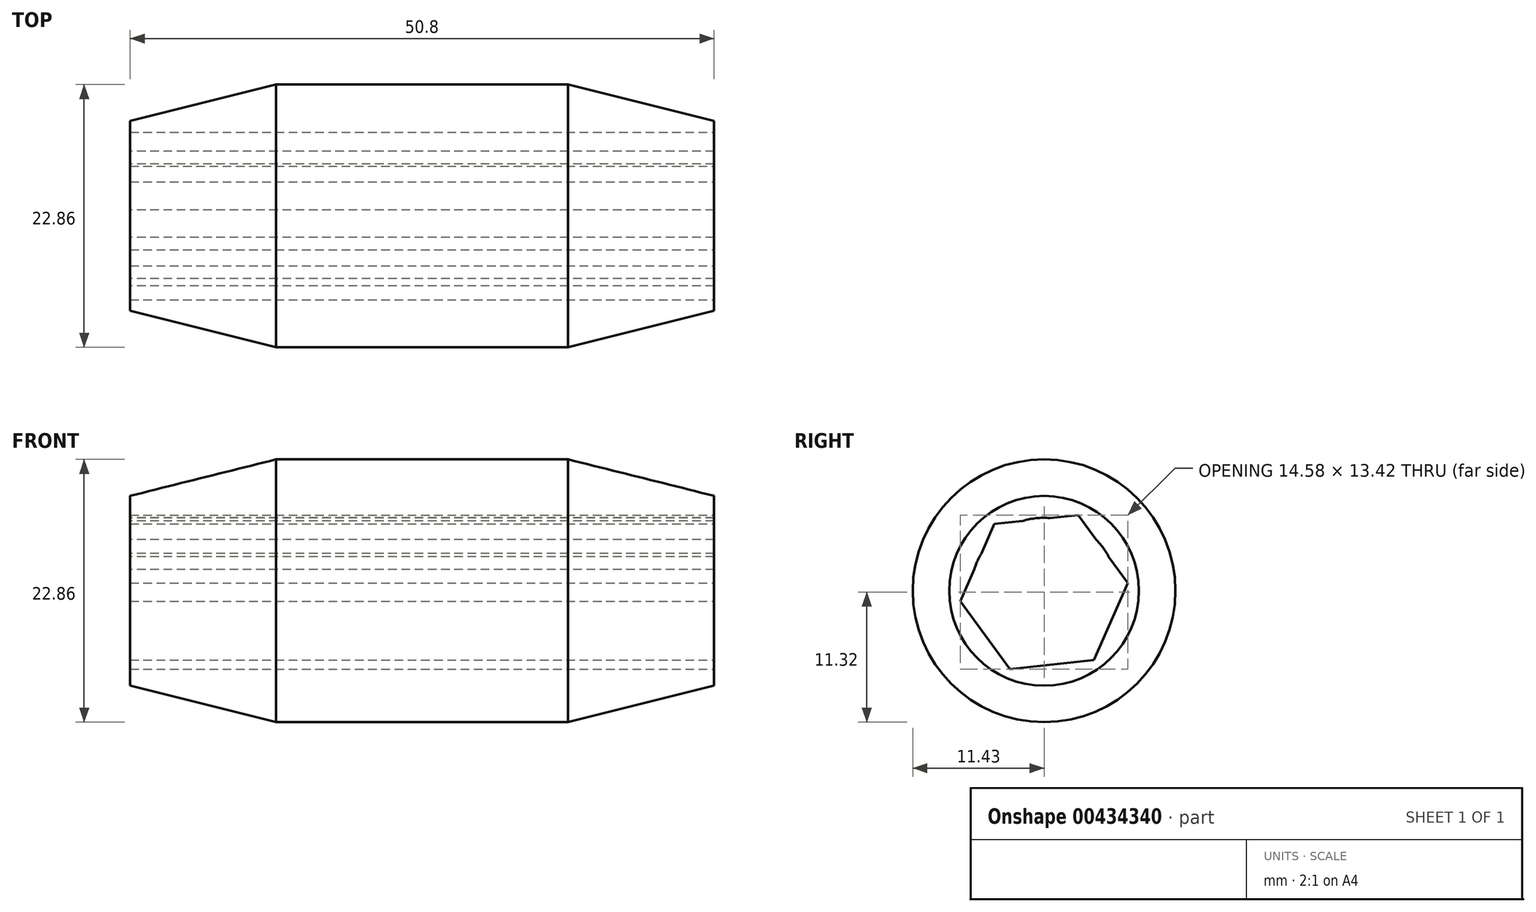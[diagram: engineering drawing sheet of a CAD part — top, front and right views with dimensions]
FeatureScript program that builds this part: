
annotation { "Feature Type Name" : "Feature", "Feature Type Description" : "" }
export const myFeature = defineFeature(function(context is Context, id is Id, definition is map)
    precondition{}
    {
        {
            var Q0;
            Q0=qCreatedBy(makeId("Right.planeOp"),FACE);
            var sketch = newSketch(context, id + "F0", { "sketchPlane" : qUnion([Q0])});
            skCircle(sketch, "E0.cCircle", {"center": v(0, 0) * mm, "radius": 6.35 * mm, "construction": true});
            skLineSegment(sketch, "E0.0", {"start": v(2.96, 6.7) * mm, "end": v(7.29, 0.8) * mm});
            skLineSegment(sketch, "E0.1", {"start": v(7.29, 0.8) * mm, "end": v(4.33, -5.92) * mm});
            skLineSegment(sketch, "E0.2", {"start": v(4.33, -5.92) * mm, "end": v(-2.96, -6.7) * mm});
            skLineSegment(sketch, "E0.3", {"start": v(-2.96, -6.7) * mm, "end": v(-7.29, -0.8) * mm});
            skLineSegment(sketch, "E0.4", {"start": v(-7.29, -0.8) * mm, "end": v(-4.33, 5.92) * mm});
            skLineSegment(sketch, "E0.5", {"start": v(-4.33, 5.92) * mm, "end": v(2.96, 6.7) * mm});
            skPoint(sketch, "E0.0.midPoint", {"position": v(5.12, 3.75) * mm});
            skSolve(sketch);
        }
        {
            var Q0;
            Q0=qCreatedBy(makeId("Front.planeOp"),FACE);
            var sketch = newSketch(context, id + "F1", { "sketchPlane" : qUnion([Q0])});
            skLineSegment(sketch, "E1", {"start": v(-42.82, 0.11) * mm, "end": v(41.93, 0.11) * mm, "construction": true});
            skLineSegment(sketch, "E2", {"start": v(-25.43, 6.46) * mm, "end": v(25.37, 6.46) * mm});
            skLineSegment(sketch, "E3", {"start": v(-12.73, 11.54) * mm, "end": v(12.67, 11.54) * mm});
            skLineSegment(sketch, "E4", {"start": v(-12.73, 11.54) * mm, "end": v(-25.43, 8.37) * mm});
            skLineSegment(sketch, "E5", {"start": v(12.67, 11.54) * mm, "end": v(25.37, 8.37) * mm});
            skLineSegment(sketch, "E6", {"start": v(25.37, 8.37) * mm, "end": v(25.37, 6.46) * mm});
            skLineSegment(sketch, "E7", {"start": v(-25.43, 8.37) * mm, "end": v(-25.43, 6.46) * mm});
            skSolve(sketch);
        }
        {
            var Q0;
            Q0 = qSketchRegion(id + "F1", true);
            var Q1;
            Q1=sQuery(id+"F1.wireOp",EDGE,"E1");
            revolve(context, id + "F2", {"entities" : qUnion([Q0]), "axis" : qUnion([Q1]), "revolveType" : RevolveType.FULL});
        }
        {
            var Q0;
            Q0 = qSketchRegion(id + "F0", true);
            extrude(context, id + "F3", {"entities" : qUnion([Q0]), "operationType" : NewBodyOperationType.REMOVE, "oppositeDirection" : true, "depth" : 38.1 * mm, "hasSecondDirection" : true, "secondDirectionOppositeDirection" : false, "secondDirectionDepth" : 38.1 * mm});
        }
    });
